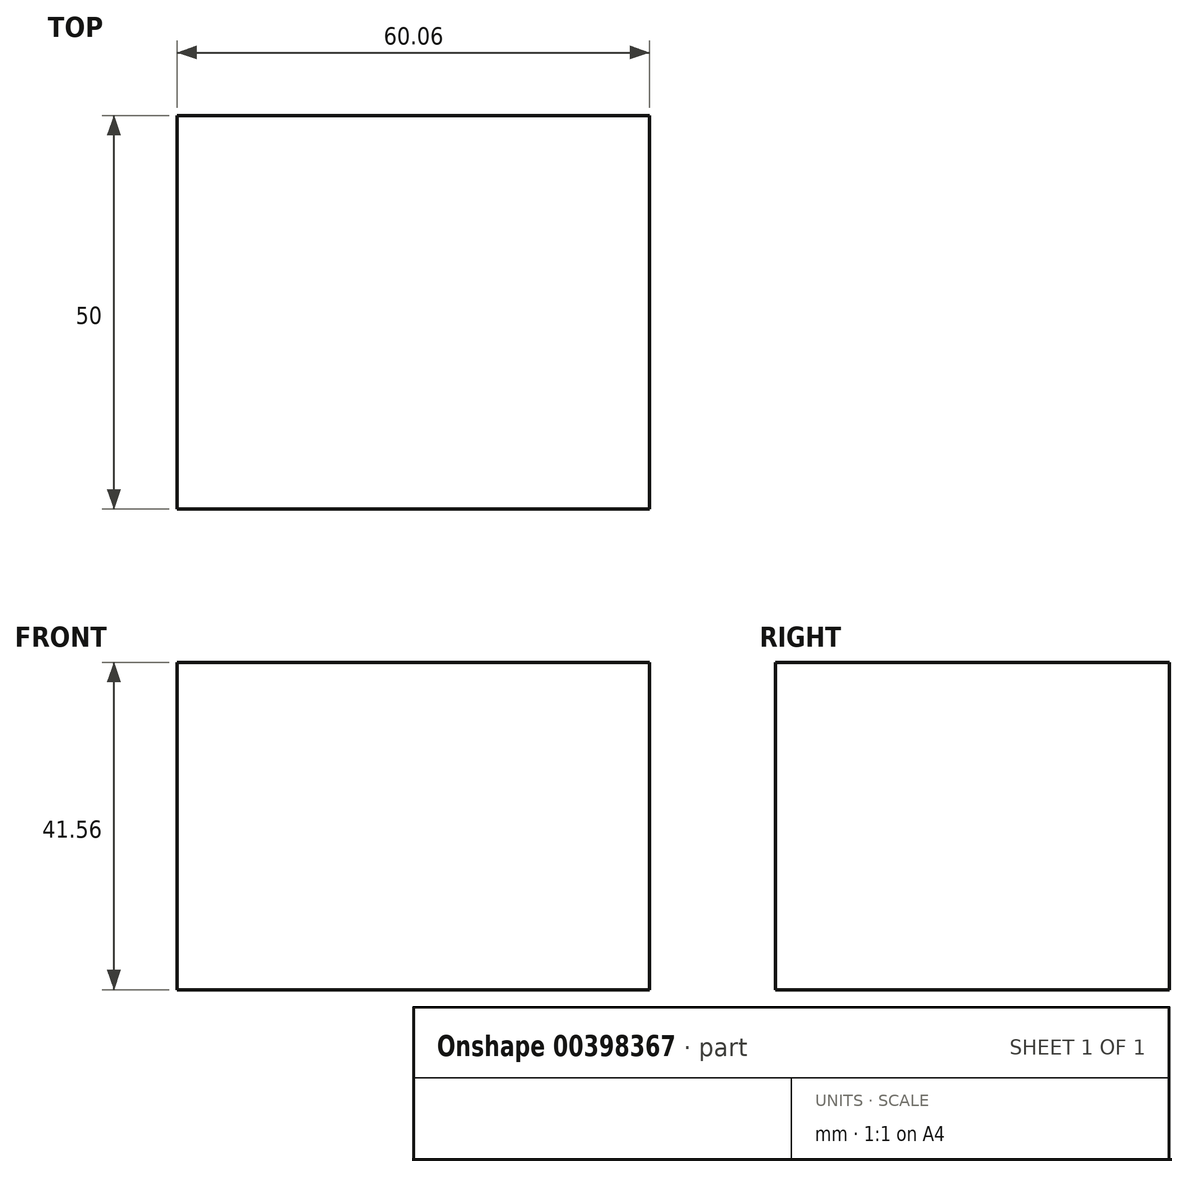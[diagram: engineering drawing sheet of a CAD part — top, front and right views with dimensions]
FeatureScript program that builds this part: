
annotation { "Feature Type Name" : "Feature", "Feature Type Description" : "" }
export const myFeature = defineFeature(function(context is Context, id is Id, definition is map)
    precondition{}
    {
        {
            var Q0;
            Q0=qCreatedBy(makeId("Front.planeOp"),FACE);
            var sketch = newSketch(context, id + "F0", { "sketchPlane" : qUnion([Q0])});
            skLineSegment(sketch, "E0.bottom", {"start": v(30.03, -20.78) * mm, "end": v(-30.03, -20.78) * mm});
            skLineSegment(sketch, "E0.top", {"start": v(30.03, 20.78) * mm, "end": v(-30.03, 20.78) * mm});
            skLineSegment(sketch, "E0.left", {"start": v(30.03, -20.78) * mm, "end": v(30.03, 20.78) * mm});
            skLineSegment(sketch, "E0.right", {"start": v(-30.03, -20.78) * mm, "end": v(-30.03, 20.78) * mm});
            skPoint(sketch, "E0.middle", {"position": v(0, 0) * mm});
            skCircle(sketch, "E1", {"center": v(-20.03, 10.78) * mm, "radius": 5 * mm});
            skCircle(sketch, "E2", {"center": v(20.03, 10.78) * mm, "radius": 5 * mm});
            skCircle(sketch, "E3", {"center": v(20.03, -10.78) * mm, "radius": 5 * mm});
            skCircle(sketch, "E4", {"center": v(-20.03, -10.78) * mm, "radius": 5 * mm});
            skSolve(sketch);
        }
        {
            var Q0;
            Q0 = qSketchRegion(id + "F0", true);
            var Q1;
            Q1=makeQuery(id+"F0.imprint","IMPRINT",FACE,{"disambiguationData":[TD([[makeQuery(id+"F0.imprint","IMPRINT",EDGE,{"derivedFrom":sQuery(id+"F0.wireOp",EDGE,"E1")}),1.0]])]});
            var Q2;
            Q2=makeQuery(id+"F0.imprint","IMPRINT",FACE,{"disambiguationData":[TD([[makeQuery(id+"F0.imprint","IMPRINT",EDGE,{"derivedFrom":sQuery(id+"F0.wireOp",EDGE,"E2")}),1.0]])]});
            var Q3;
            Q3=makeQuery(id+"F0.imprint","IMPRINT",FACE,{"disambiguationData":[TD([[makeQuery(id+"F0.imprint","IMPRINT",EDGE,{"derivedFrom":sQuery(id+"F0.wireOp",EDGE,"E3")}),1.0]])]});
            var Q4;
            Q4=makeQuery(id+"F0.imprint","IMPRINT",FACE,{"disambiguationData":[TD([[makeQuery(id+"F0.imprint","IMPRINT",EDGE,{"derivedFrom":sQuery(id+"F0.wireOp",EDGE,"E4")}),1.0]])]});
            extrude(context, id + "F1", {"entities" : qUnion([Q0, Q1, Q2, Q3, Q4]), "depth" : 50 * mm});
        }
    });
